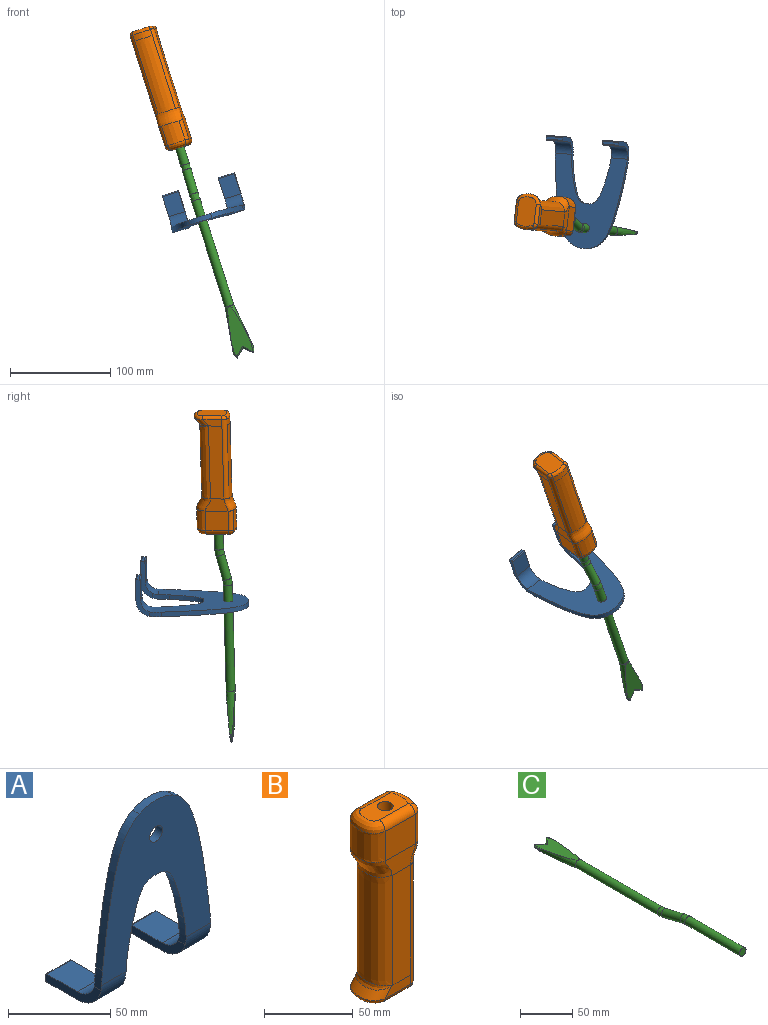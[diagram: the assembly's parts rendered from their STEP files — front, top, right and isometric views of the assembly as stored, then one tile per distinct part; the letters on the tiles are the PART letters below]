
ASSEMBLY  parts=3 mates=2
PART A: 30 faces, bbox 75.4x38.8x109.1 mm
  f0: extruded ~35.7x19.38mm, area 210.1mm2, adj f1,f6,f7,f22
  f1: extruded ~35.7x19.38mm, area 210.1mm2, adj f0,f6,f7,f23
  f2: extruded ~81.12x25.61mm, area 417.6mm2, adj f3,f6,f7,f24
  f3: cylinder r=25.4mm len=22.85mm, axis (0,-1,0), area 112.9mm2, adj f2,f4,f6,f7
  f4: extruded ~81.12x25.61mm, area 417.6mm2, adj f3,f6,f7,f25
  f5: cylinder r=4.5mm len=9mm, axis (0,-1,0), area 134.7mm2, adj f6,f7
  f6: plane 92.3x75.44mm, normal (0,-1,0), area 3891mm2, adj f0,f1,f2,f3,f4,f5,f12,f18
  f7: plane 92.3x75.44mm, normal (0,1,0), area 3891mm2, adj f0,f1,f2,f3,f4,f5,f11,f19
  f8: plane 16.82x2.76mm, normal (0,1,0), area 46.5mm2, adj f9,f10,f28,f29
  f9: plane 38.48x13.55mm, normal (-1,0,0), area 196.6mm2, adj f8,f11,f12,f13,f14,f25,f28,f29
  f10: plane 37.96x11.55mm, normal (1,0,0), area 186.6mm2, adj f8,f11,f12,f13,f14,f22,f28,f29
  f11: cylinder r=12mm len=16.96mm, axis (1,0,0), area 317.3mm2, adj f7,f9,f10,f13,f22,f25
  f12: cylinder r=16.76mm len=16.96mm, axis (1,0,0), area 443.1mm2, adj f6,f9,f10,f14,f22,f25
  f13: plane 21.03x16.82mm, normal (0,0,1), area 353.7mm2, adj f9,f10,f11,f29
  f14: plane 21.03x16.82mm, normal (0,0,-1), area 353.7mm2, adj f9,f10,f12,f28
  f15: plane 16.82x2.76mm, normal (0,1,0), area 46.5mm2, adj f16,f17,f26,f27
  f16: plane 37.96x11.55mm, normal (-1,0,0), area 186.6mm2, adj f15,f18,f19,f20,f21,f23,f26,f27
  f17: plane 38.48x13.55mm, normal (1,0,0), area 196.6mm2, adj f15,f18,f19,f20,f21,f24,f26,f27
  f18: cylinder r=16.76mm len=16.96mm, axis (1,0,0), area 443.1mm2, adj f6,f16,f17,f20,f23,f24
  f19: cylinder r=12mm len=16.96mm, axis (1,0,0), area 317.3mm2, adj f7,f16,f17,f21,f23,f24
  f20: plane 21.03x16.82mm, normal (0,0,-1), area 353.7mm2, adj f16,f17,f18,f27
  f21: plane 21.03x16.82mm, normal (0,0,1), area 353.7mm2, adj f16,f17,f19,f26
  f22: cylinder r=100mm len=17.31mm, axis (0,-1,0), area 83.5mm2, adj f0,f6,f7,f10,f11,f12
  f23: cylinder r=100mm len=17.31mm, axis (0,-1,0), area 83.5mm2, adj f1,f6,f7,f16,f18,f19
  f24: cylinder r=100mm len=11.68mm, axis (0,-1,0), area 55.9mm2, adj f2,f6,f7,f17,f18,f19
  f25: cylinder r=100mm len=11.68mm, axis (0,-1,0), area 55.9mm2, adj f4,f6,f7,f9,f11,f12
  f26: cylinder r=1mm len=16.82mm, axis (1,0,0), area 26.4mm2, adj f15,f16,f17,f21
  f27: cylinder r=1mm len=16.82mm, axis (-1,0,0), area 26.4mm2, adj f15,f16,f17,f20
  f28: cylinder r=1mm len=16.82mm, axis (-1,0,0), area 26.4mm2, adj f8,f9,f10,f14
  f29: cylinder r=1mm len=16.82mm, axis (1,0,0), area 26.4mm2, adj f8,f9,f10,f13
PART B: 37 faces, bbox 39.6x26.9x123.9 mm
  f0: bspline ~25.02x15.62mm, area 474mm2, adj f1,f3,f5,f34
  f1: bspline ~23.87x12.7mm, area 238.7mm2, adj f0,f2,f6,f35
  f2: bspline ~24.94x12.7mm, area 410.9mm2, adj f1,f3,f7,f8,f9,f27,f29,f32
  f3: bspline ~22.84x12.7mm, area 224.8mm2, adj f0,f2,f4,f33
  f4: plane 22.84x20.32mm, normal (0.01,1,0), area 464.1mm2, adj f3,f5,f9,f13
  f5: extruded ~24.97x20.32mm, area 707.6mm2, adj f0,f4,f6,f11
  f6: plane 23.87x20.32mm, normal (-0.01,-1,0), area 485mm2, adj f1,f5,f7,f12
  f7: extruded ~20.32x4.72mm, area 122.1mm2, adj f2,f6,f8,f14
  f8: extruded ~20.32x18.47mm, area 384.3mm2, adj f2,f7,f9,f16
  f9: extruded ~20.32x4.72mm, area 124.4mm2, adj f2,f4,f8,f15
  f10: plane 29.26x14.94mm, normal (0,0,1), area 347.5mm2, adj f11,f12,f13,f16,f17
  f11: bspline ~25.03x10.43mm, area 232.9mm2, adj f5,f10,f12,f13
  f12: cylinder r=5.08mm len=23.9mm, axis (-1,0.01,0), area 187.5mm2, adj f6,f10,f11,f14
  f13: cylinder r=5.08mm len=22.88mm, axis (1,-0.01,0), area 181.8mm2, adj f4,f10,f11,f15
  f14: sphere r=5.08mm, area 16.4mm2, adj f7,f12,f16
  f15: sphere r=5.08mm, area 31.1mm2, adj f9,f13,f16
  f16: bspline ~26.86x8.44mm, area 140.3mm2, adj f8,f10,f14,f15
  f17: cylinder r=4.5mm len=25.4mm, axis (0,0,1), area 717.5mm2, adj f10,f18
  f18: plane 8.99x8.99mm, normal (0,0,1), area 63.5mm2, adj f17
  f19: plane 29.35x18.72mm, normal (0,0,-1), area 507mm2, adj f20,f21,f22,f23,f24,f25
  f20: cylinder r=3.17mm len=20.16mm, axis (1,0,0), area 99.4mm2, adj f19,f21,f22,f26
  f21: bspline ~25.05x10.73mm, area 156.8mm2, adj f19,f20,f23,f31
  f22: torus R=1.91mm, axis (0,0,-1), area 23.2mm2, adj f19,f20,f24,f27
  f23: cylinder r=3.17mm len=19.02mm, axis (-1,0.01,0), area 94.6mm2, adj f19,f21,f25,f30
  f24: bspline ~19.32x5.05mm, area 90.3mm2, adj f19,f22,f25,f28
  f25: torus R=1.91mm, axis (0,0,-1), area 23.6mm2, adj f19,f23,f24,f29
  f26: bspline ~20.43x6.35mm, area 110.5mm2, adj f20,f27,f31,f35,f36
  f27: cylinder r=5.08mm len=82.55mm, axis (0,0,-1), area 496mm2, adj f2,f22,f26,f28,f32,f35
  f28: bspline ~20.62x6.35mm, area 120.4mm2, adj f24,f27,f29,f32
  f29: cylinder r=5.08mm len=82.55mm, axis (0,0,-1), area 505.5mm2, adj f2,f25,f28,f30,f32,f33
  f30: bspline ~19.18x6.35mm, area 103.1mm2, adj f23,f29,f31,f33,f36
  f31: bspline ~25.02x15.7mm, area 252.5mm2, adj f21,f26,f30,f36
  f32: extruded ~76.2x18.47mm, area 1441.5mm2, adj f2,f27,f28,f29
  f33: plane 76.21x13.52mm, normal (0.01,1,0), area 1028.4mm2, adj f3,f29,f30,f34,f36
  f34: extruded ~76.12x24.97mm, area 2655mm2, adj f0,f33,f35,f36
  f35: plane 76.25x14.83mm, normal (0,-1,0), area 1116.6mm2, adj f1,f26,f27,f34,f36
  f36: bspline ~25.16x13.1mm, area 93.9mm2, adj f26,f30,f31,f33,f34,f35
PART C: 26 faces, bbox 21.1x274x22.7 mm
  f0: cylinder r=10.41mm len=1.67mm, axis (0,-1,0), area 0.2mm2, adj f3,f14,f15
  f1: cylinder r=10.41mm len=1.67mm, axis (0,-1,0), area 0.2mm2, adj f2,f18,f19
  f2: cone r=10.41mm half-angle=7.7deg, axis (0,1,0), area 275.7mm2, adj f1,f4,f5,f18,f19,f21
  f3: cone r=10.41mm half-angle=7.7deg, axis (0,1,0), area 275.7mm2, adj f0,f4,f5,f14,f15,f21
  f4: plane 50.07x18.29mm, normal (0,0.07,1), area 611.3mm2, adj f2,f3,f8,f9,f13,f15,f16,f18
  f5: plane 50.07x18.29mm, normal (0,0.07,-1), area 611.3mm2, adj f2,f3,f10,f11,f12,f14,f17,f19
  f6: plane 1.73x1.69mm, normal (0.7,0.72,0), area 0.3mm2, adj f7,f8,f10
  f7: plane 1.73x1.69mm, normal (-0.7,0.72,0), area 0.3mm2, adj f6,f9,f11
  f8: plane 9.66x8.77mm, normal (0.48,0.54,0.69), area 18.9mm2, adj f4,f6,f9,f10,f16
  f9: plane 9.66x8.77mm, normal (-0.48,0.54,0.69), area 18.9mm2, adj f4,f7,f8,f11,f13
  f10: plane 9.66x8.77mm, normal (0.48,0.54,-0.69), area 18.9mm2, adj f5,f6,f8,f11,f17
  f11: plane 9.66x8.77mm, normal (-0.48,0.54,-0.69), area 18.9mm2, adj f5,f7,f9,f10,f12
  f12: bspline ~6.86x3.68mm, area 8.4mm2, adj f5,f11,f13,f14
  f13: bspline ~6.86x3.68mm, area 8.4mm2, adj f4,f9,f12,f15
  f14: bspline ~10.74x2.02mm, area 13mm2, adj f0,f3,f5,f12,f15
  f15: bspline ~10.74x2.02mm, area 13mm2, adj f0,f3,f4,f13,f14
  f16: bspline ~6.86x3.68mm, area 8.4mm2, adj f4,f8,f17,f18
  f17: bspline ~6.86x3.68mm, area 8.4mm2, adj f5,f10,f16,f19
  f18: bspline ~10.74x2.02mm, area 13mm2, adj f1,f2,f4,f16,f19
  f19: bspline ~10.74x2.02mm, area 13mm2, adj f1,f2,f5,f17,f18
  f20: plane 8.89x8.89mm, normal (0,-1,0), area 62.1mm2, adj f25
  f21: cylinder r=4.45mm len=110.51mm, axis (0,-1,0), area 3086.5mm2, adj f2,f3,f22
  f22: bspline ~9.32x8.81mm, area 169.3mm2, adj f21,f23
  f23: cylinder r=4.45mm len=27.35mm, axis (0,-0.97,0.24), area 725.7mm2, adj f22,f24
  f24: bspline ~9.56x8.81mm, area 169.4mm2, adj f23,f25
  f25: cylinder r=4.45mm len=73.49mm, axis (0,-1,0), area 2052.4mm2, adj f20,f24
PLACE A rot(axis=(0.97,-0.2,0.11),90.7deg) t=(-116.43,-422.03,-100.87)mm
PLACE B rot(axis=(-0.66,0.74,-0.11),167.8deg) t=(-199.38,-391.87,81.1)mm
PLACE C rot(axis=(-0.98,-0.11,-0.19),92.2deg) t=(-77.23,-473.27,-230.99)mm
MATE cylindrical C.f21 <-> A.f5  axis (-0.3,0.03,0.95) through (-107.28,-470.64,-136.51)mm
MATE cylindrical C.f25 <-> B.f17  axis (-0.3,0.03,0.95) through (-156.91,-458.7,21.61)mm
